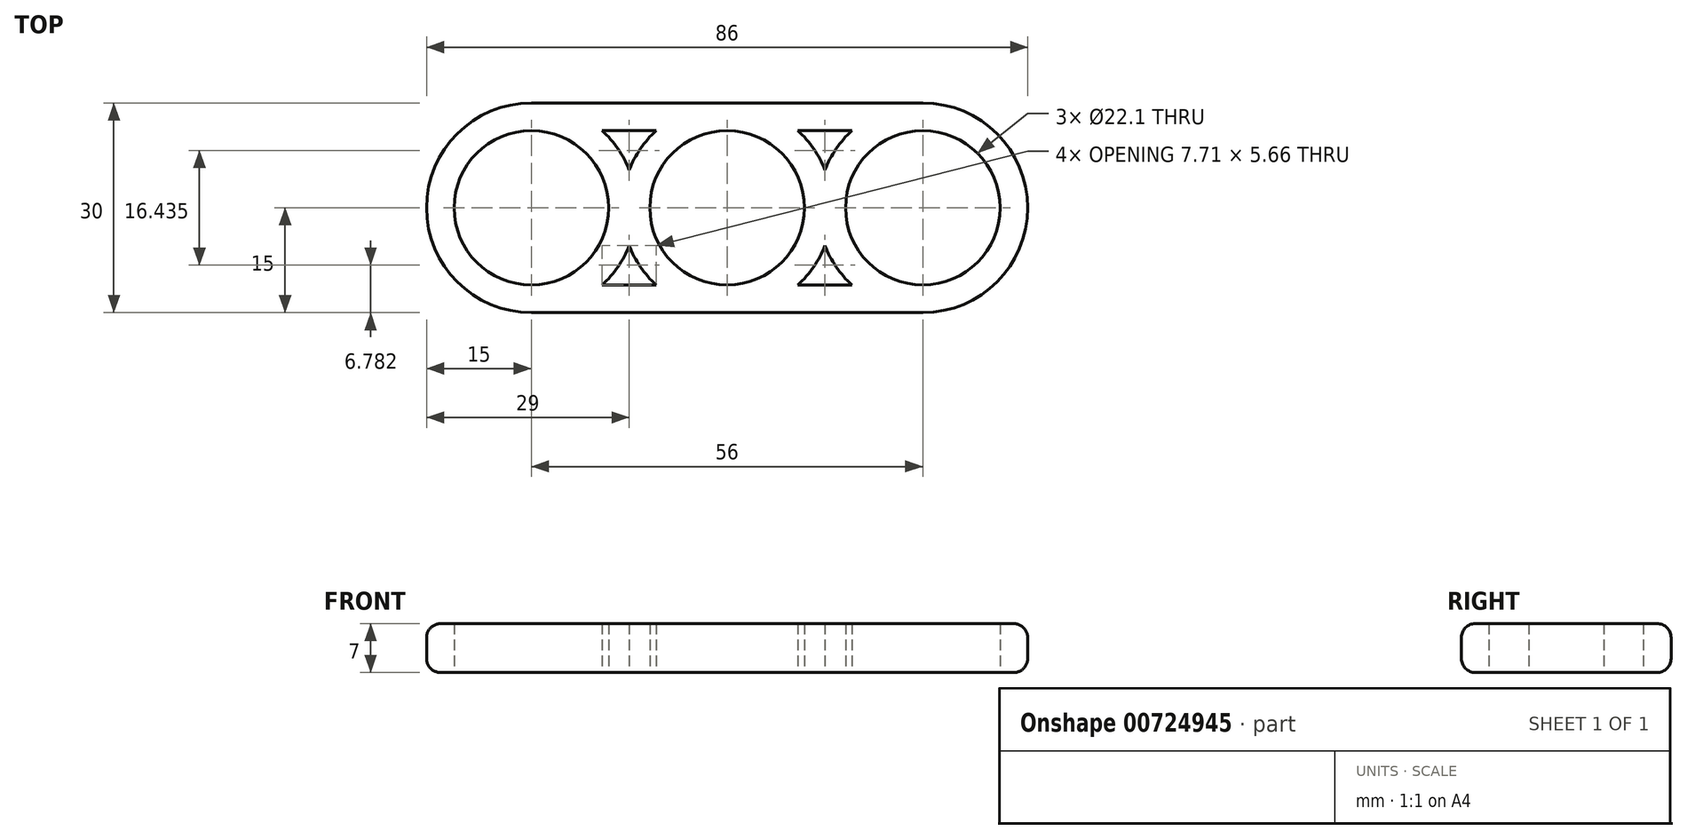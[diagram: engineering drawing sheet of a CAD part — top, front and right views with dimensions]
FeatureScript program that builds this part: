
annotation { "Feature Type Name" : "Feature", "Feature Type Description" : "" }
export const myFeature = defineFeature(function(context is Context, id is Id, definition is map)
    precondition{}
    {
        {
            var Q0;
            Q0=qCreatedBy(makeId("Top.planeOp"),FACE);
            var sketch = newSketch(context, id + "F0", { "sketchPlane" : qUnion([Q0])});
            skCircle(sketch, "E0", {"center": v(0, 0) * mm, "radius": 11.05 * mm});
            skCircle(sketch, "E1", {"center": v(0, 0) * mm, "radius": 15 * mm});
            skCircle(sketch, "E2", {"center": v(-28, 0) * mm, "radius": 11.05 * mm});
            skCircle(sketch, "E3", {"center": v(-28, 0) * mm, "radius": 15 * mm});
            skCircle(sketch, "E4", {"center": v(28, 0) * mm, "radius": 11.05 * mm});
            skCircle(sketch, "E5", {"center": v(28, 0) * mm, "radius": 15 * mm});
            skLineSegment(sketch, "E6", {"start": v(-28, 0) * mm, "end": v(-28, -15) * mm, "construction": true});
            skLineSegment(sketch, "E7", {"start": v(-28, 0) * mm, "end": v(-28, 15) * mm, "construction": true});
            skLineSegment(sketch, "E8", {"start": v(28, 0) * mm, "end": v(28, 15) * mm, "construction": true});
            skLineSegment(sketch, "E9", {"start": v(28, 0) * mm, "end": v(28, -15) * mm, "construction": true});
            skLineSegment(sketch, "E10", {"start": v(-28, -15) * mm, "end": v(28, -15) * mm});
            skLineSegment(sketch, "E11", {"start": v(-28, 15) * mm, "end": v(28, 15) * mm});
            skPoint(sketch, "E12.endSnap0", {"position": v(28, -7.5) * mm});
            skLineSegment(sketch, "E13", {"start": v(-17.86, -11.05) * mm, "end": v(17.86, -11.05) * mm});
            skLineSegment(sketch, "E14", {"start": v(-17.86, 11.05) * mm, "end": v(17.86, 11.05) * mm});
            skSolve(sketch);
        }
        {
            var Q0;
            Q0 = qSketchRegion(id + "F0", true);
            var Q1;
            {var subQ0=sQuery(id+"F0.wireOp",EDGE,"E3");var subQ1=sQuery(id+"F0.wireOp",EDGE,"E1");var subQ2=makeQuery(id+"F0.imprint","INTERSECT",VERTEX,{"disambiguationData":[OD(0.0)],"derivedFrom":[subQ1,subQ0]});Q1=makeQuery(id+"F0.imprint","IMPRINT",FACE,{"disambiguationData":[TD([[makeQuery(id+"F0.imprint","IMPRINT",EDGE,{"disambiguationData":[TD([[subQ2,-1.0]])],"derivedFrom":subQ1}),1.0]])]});}
            var Q2;
            {var subQ4=sQuery(id+"F0.wireOp",EDGE,"E13");var subQ8=sQuery(id+"F0.wireOp",EDGE,"E0");var subQ9=makeQuery(id+"F0.imprint","INTERSECT",VERTEX,{"derivedFrom":[subQ8,subQ4]});Q2=makeQuery(id+"F0.imprint","IMPRINT",FACE,{"disambiguationData":[TD([[makeQuery(id+"F0.imprint","IMPRINT",EDGE,{"disambiguationData":[TD([[subQ9,1.0]])],"derivedFrom":subQ8}),-1.0]])]});}
            var Q3;
            {var subQ0=sQuery(id+"F0.wireOp",EDGE,"E13");var subQ5=sQuery(id+"F0.wireOp",EDGE,"E0");var subQ6=makeQuery(id+"F0.imprint","INTERSECT",VERTEX,{"derivedFrom":[subQ5,subQ0]});Q3=makeQuery(id+"F0.imprint","IMPRINT",FACE,{"disambiguationData":[TD([[makeQuery(id+"F0.imprint","IMPRINT",EDGE,{"disambiguationData":[TD([[subQ6,-1.0]])],"derivedFrom":subQ5}),-1.0]])]});}
            var Q4;
            {var subQ0=sQuery(id+"F0.wireOp",EDGE,"E5");var subQ1=sQuery(id+"F0.wireOp",EDGE,"E1");var subQ2=makeQuery(id+"F0.imprint","INTERSECT",VERTEX,{"disambiguationData":[OD(0.0)],"derivedFrom":[subQ1,subQ0]});Q4=makeQuery(id+"F0.imprint","IMPRINT",FACE,{"disambiguationData":[TD([[makeQuery(id+"F0.imprint","IMPRINT",EDGE,{"disambiguationData":[TD([[subQ2,1.0]])],"derivedFrom":subQ1}),1.0]])]});}
            extrude(context, id + "F1", {"entities" : qUnion([Q0, Q1, Q2, Q3, Q4]), "depth" : 7 * mm, "offsetDistance" : 25 * mm});
        }
        {
            var Q0;
            Q0=makeQuery(id+"F1.opExtrude","CAP_EDGE",EDGE,{"disambiguationData":[OSD([sQuery(id+"F0.wireOp",EDGE,"E11")])],"isStart":false});
            var Q1;
            Q1=makeQuery(id+"F1.opExtrude","CAP_EDGE",EDGE,{"disambiguationData":[OSD([sQuery(id+"F0.wireOp",EDGE,"E10")])],"isStart":true});
            fillet(context, id + "F2", {"entities" : qUnion([Q0, Q1]), "radius" : 2 * mm, "tangentPropagation" : true, "allowEdgeOverflow" : false});
        }
    });
